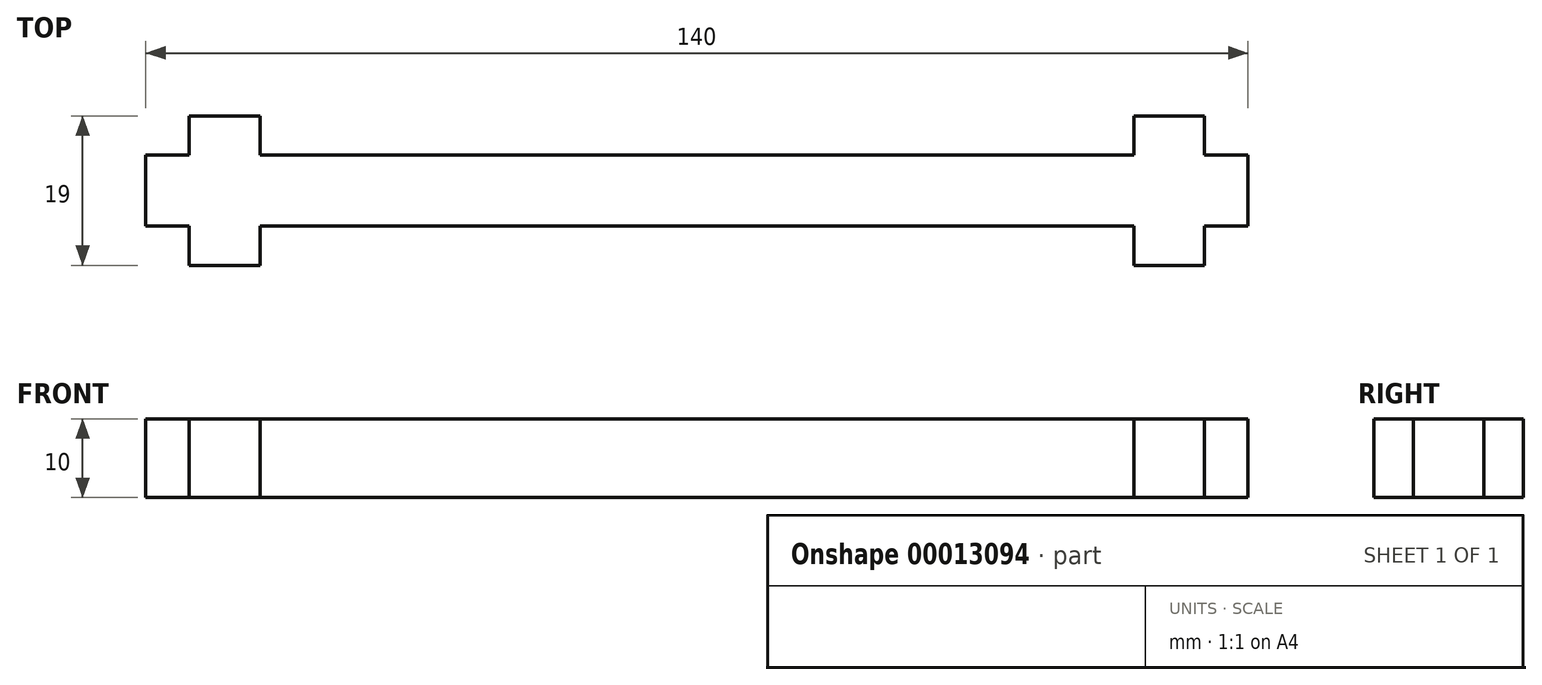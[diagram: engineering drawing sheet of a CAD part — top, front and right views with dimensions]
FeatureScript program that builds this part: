
annotation { "Feature Type Name" : "Feature", "Feature Type Description" : "" }
export const myFeature = defineFeature(function(context is Context, id is Id, definition is map)
    precondition{}
    {
        {
            var Q0;
            Q0=qCreatedBy(makeId("Top.planeOp"),FACE);
            var sketch = newSketch(context, id + "F0", { "sketchPlane" : qUnion([Q0])});
            skLineSegment(sketch, "E0", {"start": v(-8.08, 70.3) * mm, "end": v(-8.08, -17.44) * mm, "construction": true});
            skLineSegment(sketch, "E1", {"start": v(-8.08, 26.43) * mm, "end": v(-108.1, 26.43) * mm, "construction": true});
            skPoint(sketch, "E2", {"position": v(-8.08, 30.93) * mm});
            skLineSegment(sketch, "E3", {"start": v(-8.08, 30.93) * mm, "end": v(-63.58, 30.93) * mm});
            skLineSegment(sketch, "E4", {"start": v(-63.58, 30.93) * mm, "end": v(-63.58, 35.93) * mm});
            skLineSegment(sketch, "E5", {"start": v(-63.58, 35.93) * mm, "end": v(-72.58, 35.93) * mm});
            skLineSegment(sketch, "E6", {"start": v(-72.58, 35.93) * mm, "end": v(-72.58, 30.93) * mm});
            skLineSegment(sketch, "E7", {"start": v(-72.58, 30.93) * mm, "end": v(-78.08, 30.93) * mm});
            skLineSegment(sketch, "E8", {"start": v(-78.08, 30.93) * mm, "end": v(-78.08, 26.43) * mm});
            skLineSegment(sketch, "E9.0.MirrorCS", {"start": v(-8.08, 21.93) * mm, "end": v(-63.58, 21.93) * mm});
            skLineSegment(sketch, "E9.1.MirrorCS", {"start": v(-63.58, 21.93) * mm, "end": v(-63.58, 16.93) * mm});
            skLineSegment(sketch, "E9.2.MirrorCS", {"start": v(-63.58, 16.93) * mm, "end": v(-72.58, 16.93) * mm});
            skLineSegment(sketch, "E9.3.MirrorCS", {"start": v(-72.58, 16.93) * mm, "end": v(-72.58, 21.93) * mm});
            skLineSegment(sketch, "E9.4.MirrorCS", {"start": v(-78.08, 21.93) * mm, "end": v(-78.08, 26.43) * mm});
            skLineSegment(sketch, "E9.5.MirrorCS", {"start": v(-72.58, 21.93) * mm, "end": v(-78.08, 21.93) * mm});
            skLineSegment(sketch, "E10.0.MirrorCS", {"start": v(-8.08, 30.93) * mm, "end": v(47.42, 30.93) * mm});
            skLineSegment(sketch, "E11.0.MirrorCS", {"start": v(47.42, 30.93) * mm, "end": v(47.42, 35.93) * mm});
            skLineSegment(sketch, "E12.0.MirrorCS", {"start": v(47.42, 35.93) * mm, "end": v(56.42, 35.93) * mm});
            skLineSegment(sketch, "E13.0.MirrorCS", {"start": v(56.42, 35.93) * mm, "end": v(56.42, 30.93) * mm});
            skLineSegment(sketch, "E14.0.MirrorCS", {"start": v(56.42, 30.93) * mm, "end": v(61.92, 30.93) * mm});
            skLineSegment(sketch, "E15.0.MirrorCS", {"start": v(61.92, 30.93) * mm, "end": v(61.92, 26.43) * mm});
            skLineSegment(sketch, "E16.0.MirrorCS", {"start": v(61.92, 21.93) * mm, "end": v(61.92, 26.43) * mm});
            skLineSegment(sketch, "E17.0.MirrorCS", {"start": v(56.42, 21.93) * mm, "end": v(61.92, 21.93) * mm});
            skLineSegment(sketch, "E18.0.MirrorCS", {"start": v(56.42, 16.93) * mm, "end": v(56.42, 21.93) * mm});
            skLineSegment(sketch, "E19.0.MirrorCS", {"start": v(47.42, 16.93) * mm, "end": v(56.42, 16.93) * mm});
            skLineSegment(sketch, "E20.0.MirrorCS", {"start": v(47.42, 21.93) * mm, "end": v(47.42, 16.93) * mm});
            skLineSegment(sketch, "E21.0.MirrorCS", {"start": v(-8.08, 21.93) * mm, "end": v(47.42, 21.93) * mm});
            skSolve(sketch);
        }
        {
            var Q0;
            Q0=makeQuery(id+"F0.imprint","IMPRINT",FACE,{"disambiguationData":[TD([[makeQuery(id+"F0.imprint","IMPRINT",EDGE,{"derivedFrom":sQuery(id+"F0.wireOp",EDGE,"E3")}),1.0]])]});
            extrude(context, id + "F1", {"entities" : qUnion([Q0]), "depth" : 10 * mm});
        }
    });
